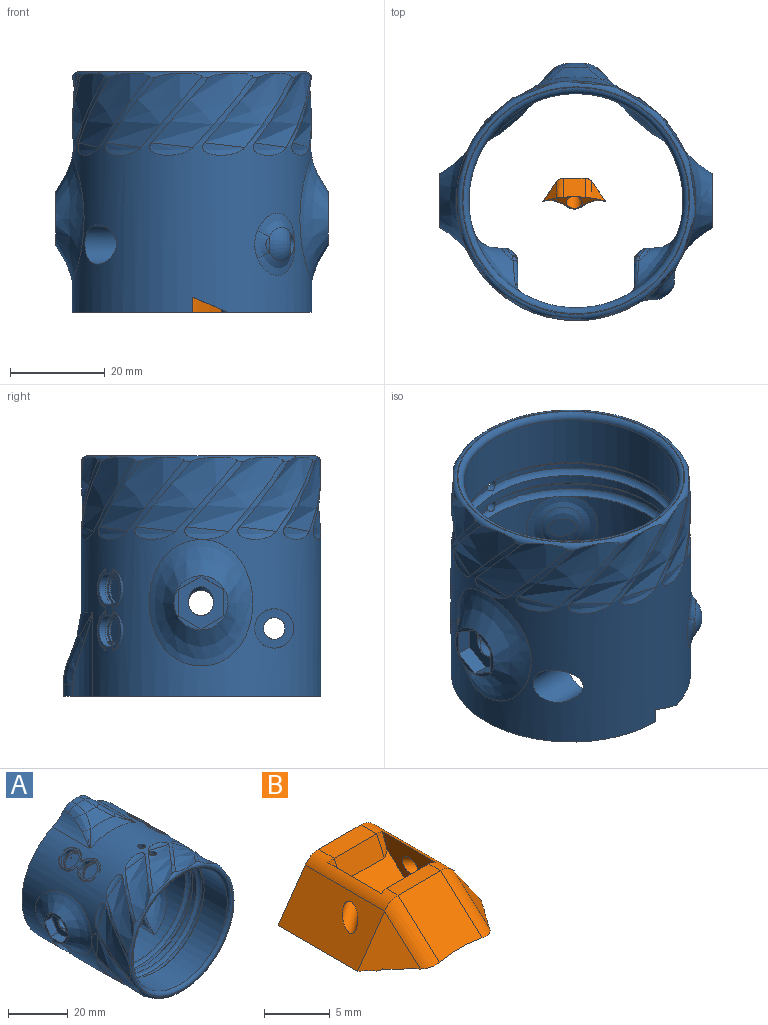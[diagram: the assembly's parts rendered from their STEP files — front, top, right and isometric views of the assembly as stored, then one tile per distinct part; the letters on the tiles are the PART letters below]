
ASSEMBLY  parts=2 mates=1
PART A: 254 faces, bbox 63.8x60.4x65 mm
  f0: cylinder r=3.37mm len=6.73mm, axis (0.64,0,0.77), area 10.5mm2, adj f1,f250,f251
  f1: torus R=20.91mm, axis (-0.55,-0.83,-0.04), area 47.7mm2, adj f0,f2,f3,f4,f249,f250
  f2: cylinder r=3.81mm len=7.62mm, axis (-0.64,0,-0.77), area 22.9mm2, adj f1,f3,f250
  f3: plane 7.63x5.85mm, normal (-0.64,0,-0.77), area 9.6mm2, adj f1,f2,f4
  f4: cylinder r=3.37mm len=6.73mm, axis (0.64,0,0.77), area 34.9mm2, adj f1,f3,f5,f7,f248
  f5: plane 9.44x3.14mm, normal (0.64,0,0.77), area 6.4mm2, adj f4,f6,f7
  f6: bspline ~8.68x3.45mm, area 0.1mm2, adj f5,f7
  f7: cylinder r=25.31mm len=50.62mm, axis (0,1,0), area 3905.4mm2, adj f4,f5,f6,f8,f168,f169,f170,f171
  f8: cylinder r=4.15mm len=11.06mm, axis (-1,0,0), area 190.1mm2, adj f7,f9,f161,f162,f163,f164,f165,f166
  f9: cylinder r=22.64mm len=45.29mm, axis (0,1,0), area 2204.6mm2, adj f8,f10,f32,f33,f34,f35,f50,f65
  f10: cylinder r=4.15mm len=8.31mm, axis (-1,0,0), area 147.8mm2, adj f9,f11,f24,f25,f26,f27,f28,f32
  f11: cylinder r=1.27mm len=1.9mm, axis (0,-1,0), area 0.9mm2, adj f10,f12,f24,f27
  f12: bspline ~1.21x1.2mm, area 0.4mm2, adj f11,f13,f23
  f13: bspline ~7.99x2.24mm, area 9.1mm2, adj f12,f14,f21,f22,f23,f27
  f14: cylinder r=5.42mm len=9.09mm, axis (-1,0,0), area 10.2mm2, adj f13,f15,f18,f33
  f15: torus R=4.41mm, axis (1,0,0), area 1.3mm2, adj f14,f16,f23,f24
  f16: bspline ~6.55x4.88mm, area 8.1mm2, adj f15,f17,f24,f33
  f17: bspline ~5.6x2.57mm, area 2.4mm2, adj f16,f32,f33
  f18: torus R=4.41mm, axis (1,0,0), area 1.3mm2, adj f14,f19,f21,f25
  f19: bspline ~6.55x4.88mm, area 8.1mm2, adj f18,f20,f25,f33
  f20: bspline ~4.89x2.08mm, area 2.4mm2, adj f19,f33,f34
  f21: bspline ~1.33x1.3mm, area 0.3mm2, adj f13,f18,f22,f25
  f22: bspline ~1.21x1.2mm, area 0.4mm2, adj f13,f21,f26
  f23: bspline ~1.05x0.91mm, area 0.3mm2, adj f12,f13,f15,f24
  f24: plane 5.75x4.22mm, normal (-1,0,0), area 6.7mm2, adj f10,f11,f15,f16,f23,f32
  f25: plane 5.74x4.21mm, normal (-1,0,0), area 6.7mm2, adj f10,f18,f19,f21,f26,f34
  f26: cylinder r=1.27mm len=1.9mm, axis (0,-1,0), area 0.9mm2, adj f10,f22,f25,f27
  f27: plane 6x1.48mm, normal (-0.71,0,0.71), area 5.5mm2, adj f10,f11,f13,f26
  f28: plane 8.31x8.31mm, normal (-1,0,0), area 37.8mm2, adj f10,f29
  f29: cylinder r=2.29mm len=4.57mm, axis (-1,0,0), area 44.4mm2, adj f28,f30,f168,f169,f170
  f30: torus R=0.85mm, axis (1,0,0), area 38mm2, adj f29,f31,f168,f170
  f31: cylinder r=5.42mm len=3.31mm, axis (-1,0,0), area 0mm2, adj f30,f171
  f32: cylinder r=1.52mm len=10.75mm, axis (0,1,0), area 11.5mm2, adj f9,f10,f17,f24
  f33: bspline ~24.01x16.87mm, area 259.2mm2, adj f9,f14,f16,f17,f19,f20,f34
  f34: cylinder r=1.52mm len=10.75mm, axis (0,1,0), area 10.8mm2, adj f9,f10,f20,f25,f33
  f35: cylinder r=5.71mm len=11.43mm, axis (1,0,0), area 14mm2, adj f9,f36
  f36: plane 17.21x17.21mm, normal (1,0,0), area 73.2mm2, adj f35,f37,f49
  f37: cylinder r=2.67mm len=5.33mm, axis (1,0,0), area 19.9mm2, adj f36,f38,f39,f49
  f38: cylinder r=2.63mm len=5.26mm, axis (-0.87,-0.49,0), area 0mm2, adj f37,f39
  f39: plane 14x12.51mm, normal (-1,0,0), area 55mm2, adj f37,f38,f40,f44,f45,f46,f47,f48
  f40: plane 5.17x3.77mm, normal (0,0.87,-0.5), area 19mm2, adj f39,f41,f43,f44,f48
  f41: plane 11.87x11.87mm, normal (-1,0,0), area 21.8mm2, adj f40,f42,f43,f44,f45,f46,f47,f48
  f42: cylinder r=2.63mm len=1.05mm, axis (-0.87,-0.49,0), area 0mm2, adj f41,f44
  f43: cylinder r=2.63mm len=1.05mm, axis (-0.87,-0.49,0), area 0mm2, adj f40,f41
  f44: plane 5.11x3.71mm, normal (0,0.87,0.5), area 19mm2, adj f39,f40,f41,f42,f45
  f45: plane 5.57x3.43mm, normal (0,0,1), area 19.1mm2, adj f39,f41,f44,f46
  f46: plane 4.83x3.43mm, normal (0,-0.87,0.5), area 19.1mm2, adj f39,f41,f45,f47
  f47: plane 4.83x3.43mm, normal (0,-0.87,-0.5), area 19.1mm2, adj f39,f41,f46,f48
  f48: plane 5.57x3.43mm, normal (0,0,-1), area 19.1mm2, adj f39,f40,f41,f47
  f49: cylinder r=2.63mm len=5.26mm, axis (-0.87,-0.49,0), area 0mm2, adj f36,f37
  f50: cylinder r=5.71mm len=11.43mm, axis (1,0,0), area 14mm2, adj f9,f51
  f51: plane 17.21x17.21mm, normal (-1,0,0), area 73.2mm2, adj f50,f52,f53
  f52: cylinder r=2.63mm len=5.26mm, axis (0.87,-0.49,0), area 0mm2, adj f51,f53
  f53: cylinder r=2.67mm len=5.33mm, axis (1,0,0), area 19.9mm2, adj f51,f52,f54,f64
  f54: plane 14x12.51mm, normal (1,0,0), area 55mm2, adj f53,f55,f59,f60,f61,f62,f63,f64
  f55: plane 4.83x3.43mm, normal (0,-0.87,-0.5), area 19.1mm2, adj f54,f56,f59,f63
  f56: plane 11.92x11.92mm, normal (1,0,0), area 21.8mm2, adj f55,f57,f58,f59,f60,f61,f62,f63
  f57: cylinder r=2.63mm len=1.05mm, axis (0.87,-0.49,0), area 0mm2, adj f56,f62
  f58: cylinder r=2.63mm len=1.05mm, axis (0.87,-0.49,0), area 0mm2, adj f56,f61
  f59: plane 4.83x3.43mm, normal (0,-0.87,0.5), area 19.1mm2, adj f54,f55,f56,f60
  f60: plane 5.57x3.43mm, normal (0,0,1), area 19.1mm2, adj f54,f56,f59,f61
  f61: plane 5.17x3.77mm, normal (0,0.87,0.5), area 19mm2, adj f54,f56,f58,f60,f62
  f62: plane 5.11x3.71mm, normal (0,0.87,-0.5), area 19mm2, adj f54,f56,f57,f61,f63
  f63: plane 5.57x3.43mm, normal (0,0,-1), area 19.1mm2, adj f54,f55,f56,f62
  f64: cylinder r=2.63mm len=5.26mm, axis (0.87,-0.49,0), area 0mm2, adj f53,f54
  f65: torus R=23.03mm, axis (0,-1,0), area 25.4mm2, adj f9,f66,f246,f247
  f66: bspline ~3.15x2.37mm, area 1.3mm2, adj f65,f67,f73,f247
  f67: bspline ~13.04x11.86mm, area 11.2mm2, adj f66,f68,f72,f247
  f68: bspline ~35.8x17.93mm, area 139.6mm2, adj f67,f69,f71,f73,f88
  f69: bspline ~3.19x1.63mm, area 2.1mm2, adj f68,f70,f75,f88
  f70: bspline ~4.55x2.66mm, area 4.6mm2, adj f69,f71,f74,f75
  f71: bspline ~4.25x3.15mm, area 6.9mm2, adj f68,f70,f74
  f72: bspline ~2.23x0.82mm, area 0.6mm2, adj f67,f88,f89,f247
  f73: bspline ~19.65x5.91mm, area 17.5mm2, adj f9,f66,f68,f74
  f74: bspline ~1.37x1.08mm, area 0.8mm2, adj f9,f70,f71,f73
  f75: bspline ~24.01x16.87mm, area 247.8mm2, adj f9,f69,f70,f76,f77,f85,f86,f87
  f76: bspline ~4.89x2.08mm, area 2.4mm2, adj f75,f77,f161
  f77: bspline ~6.55x4.88mm, area 8.1mm2, adj f75,f76,f78,f162
  f78: torus R=4.41mm, axis (1,0,0), area 1.3mm2, adj f77,f79,f85,f162
  f79: bspline ~1.28x1.27mm, area 0.3mm2, adj f78,f80,f81,f162
  f80: bspline ~1.21x1.2mm, area 0.4mm2, adj f79,f81,f163
  f81: bspline ~7.99x2.24mm, area 9.1mm2, adj f79,f80,f82,f83,f85,f164
  f82: bspline ~1.21x1.2mm, area 0.4mm2, adj f81,f83,f165
  f83: bspline ~1.33x1.3mm, area 0.3mm2, adj f81,f82,f84,f166
  f84: torus R=4.41mm, axis (1,0,0), area 1.3mm2, adj f83,f85,f86,f166
  f85: cylinder r=5.42mm len=9.09mm, axis (-1,0,0), area 10.2mm2, adj f75,f78,f81,f84
  f86: bspline ~6.55x4.88mm, area 8.1mm2, adj f75,f84,f87,f166
  f87: bspline ~5.6x2.57mm, area 2.4mm2, adj f75,f86,f167
  f88: bspline ~29.98x15.71mm, area 33.2mm2, adj f9,f68,f69,f72
  f89: torus R=23.03mm, axis (0,-1,0), area 1.1mm2, adj f9,f72,f90,f247
  f90: plane 8.88x4.76mm, normal (0.82,0,-0.57), area 41mm2, adj f9,f89,f91,f107,f108,f109,f247
  f91: plane 0.89x0.87mm, normal (-0.23,-0.65,0.72), area 0.3mm2, adj f90,f92,f107,f117
  f92: plane 4.06x3.42mm, normal (-0.16,-0.99,0.04), area 1.4mm2, adj f91,f93,f106,f107,f117
  f93: plane 8.23x0.69mm, normal (0,-0.74,-0.67), area 0.7mm2, adj f92,f94,f97,f98,f105,f106,f108,f117
  f94: plane 4.06x3.42mm, normal (0.16,-0.99,0.04), area 1.4mm2, adj f93,f95,f96,f97,f148
  f95: plane 0.89x0.87mm, normal (0.23,-0.65,0.72), area 0.3mm2, adj f94,f96,f148,f249
  f96: plane 4.19x2.94mm, normal (0.73,-0.46,0.51), area 1mm2, adj f94,f95,f97,f98,f249
  f97: extruded ~0.4x0.32mm, area 0mm2, adj f93,f94,f96,f98
  f98: cylinder r=2.03mm len=8.49mm, axis (0,1,0), area 14.4mm2, adj f93,f96,f97,f99,f102,f103,f104,f105
  f99: plane 5.9x0.63mm, normal (0,0.67,-0.74), area 3.7mm2, adj f98,f100,f101,f102,f105,f108
  f100: cylinder r=1.27mm len=5.84mm, axis (-1,0,0), area 11.7mm2, adj f99,f101,f102,f103
  f101: plane 2.76x0.85mm, normal (1,0,0), area 1.5mm2, adj f99,f100,f103,f108
  f102: plane 2.76x0.85mm, normal (-1,0,0), area 1.5mm2, adj f98,f99,f100,f103
  f103: plane 5.89x0.48mm, normal (0,-0.74,-0.67), area 2.6mm2, adj f98,f100,f101,f102,f104,f108
  f104: plane 4.57x4.45mm, normal (0,0,-1), area 20.3mm2, adj f98,f103,f108,f247
  f105: plane 4.57x1.49mm, normal (0,0,-1), area 6.8mm2, adj f93,f98,f99,f108
  f106: extruded ~0.4x0.32mm, area 0mm2, adj f92,f93,f107,f108
  f107: plane 4.19x2.94mm, normal (-0.73,-0.46,0.51), area 1mm2, adj f90,f91,f92,f106,f108
  f108: cylinder r=2.03mm len=8.49mm, axis (0,1,0), area 14.4mm2, adj f90,f93,f99,f101,f103,f104,f105,f106
  f109: torus R=20.91mm, axis (0.55,-0.83,-0.04), area 47.7mm2, adj f90,f110,f114,f115,f116,f184
  f110: cylinder r=3.37mm len=6.73mm, axis (-0.64,0,0.77), area 10.3mm2, adj f109,f111,f114
  f111: plane 6.73x5.16mm, normal (-0.64,0,0.77), area 35.5mm2, adj f110,f112,f113
  f112: plane 0.45x0.13mm, normal (0.56,0.34,0.75), area 0mm2, adj f111,f113
  f113: torus R=20.91mm, axis (0.55,-0.83,-0.04), area 0.1mm2, adj f111,f112
  f114: plane 7.62x5.84mm, normal (-0.64,0,0.77), area 9.5mm2, adj f109,f110,f115
  f115: cylinder r=3.81mm len=7.62mm, axis (-0.64,0,0.77), area 22.9mm2, adj f109,f114,f116
  f116: plane 7.63x5.85mm, normal (0.64,0,-0.77), area 9.6mm2, adj f109,f115,f184
  f117: plane 5.1x5.03mm, normal (0.73,0.46,-0.51), area 16.4mm2, adj f9,f91,f92,f93,f118
  f118: extruded ~5.22x4.81mm, area 11.5mm2, adj f9,f93,f117,f146
  f119: bspline ~14.5x11.6mm, area 84.2mm2, adj f9,f120,f126
  f120: bspline ~9.25x6.81mm, area 40.2mm2, adj f119,f121,f122
  f121: plane 4.62x4.52mm, normal (0.64,0,-0.77), area 21.6mm2, adj f120,f122
  f122: bspline ~4.17x3.65mm, area 6.9mm2, adj f120,f121,f123
  f123: bspline ~4.22x3.72mm, area 6.9mm2, adj f122,f124,f125
  f124: bspline ~9.25x6.81mm, area 40.2mm2, adj f123,f125,f126
  f125: plane 4.62x4.52mm, normal (0.64,0,-0.77), area 21.6mm2, adj f123,f124
  f126: bspline ~14.2x11.6mm, area 84.2mm2, adj f9,f119,f124,f135
  f127: bspline ~14.5x11.61mm, area 84.2mm2, adj f9,f128,f134
  f128: bspline ~9.25x6.81mm, area 40.2mm2, adj f127,f129,f130
  f129: plane 4.62x4.52mm, normal (-0.64,0,-0.77), area 21.6mm2, adj f128,f130
  f130: bspline ~4.17x3.68mm, area 6.9mm2, adj f128,f129,f131
  f131: bspline ~4.22x3.7mm, area 6.9mm2, adj f130,f132,f133
  f132: bspline ~9.25x6.81mm, area 40.2mm2, adj f131,f133,f134
  f133: plane 4.62x4.52mm, normal (-0.64,0,-0.77), area 21.6mm2, adj f131,f132
  f134: bspline ~14.2x11.6mm, area 84.2mm2, adj f9,f127,f132,f135
  f135: torus R=22.14mm, axis (0,1,0), area 243.9mm2, adj f9,f126,f134,f136,f242
  f136: cylinder r=23.81mm len=47.63mm, axis (0,1,0), area 174.6mm2, adj f135,f137,f242
  f137: torus R=22.14mm, axis (0,1,0), area 244.3mm2, adj f136,f138,f242
  f138: cylinder r=22.64mm len=45.29mm, axis (0,1,0), area 274.1mm2, adj f137,f139
  f139: torus R=22.14mm, axis (0,1,0), area 244.3mm2, adj f138,f140,f145
  f140: cylinder r=23.81mm len=47.63mm, axis (0,1,0), area 174.5mm2, adj f139,f141,f145
  f141: torus R=22.14mm, axis (0,1,0), area 244.3mm2, adj f140,f142,f145
  f142: cylinder r=22.64mm len=45.29mm, axis (0,1,0), area 1564.5mm2, adj f141,f143
  f143: torus R=23.91mm, axis (0,1,0), area 289.6mm2, adj f142,f144
  f144: plane 48.08x48.08mm, normal (0,-1,0), area 19.1mm2, adj f143,f236
  f145: cylinder r=1.27mm len=2.54mm, axis (0,0,-1), area 10.9mm2, adj f139,f140,f141,f240
  f146: plane 4.93x4.71mm, normal (0,0.67,-0.74), area 29mm2, adj f9,f93,f118,f147
  f147: extruded ~5.22x4.81mm, area 11.5mm2, adj f9,f93,f146,f148
  f148: plane 5.1x5.03mm, normal (-0.73,0.46,-0.51), area 16.4mm2, adj f9,f93,f94,f95,f147
  f149: torus R=23.03mm, axis (0,-1,0), area 20.1mm2, adj f9,f150,f247,f249
  f150: bspline ~3.31x2.12mm, area 1.3mm2, adj f149,f151,f155,f247
  f151: bspline ~13.96x10.82mm, area 11.2mm2, adj f150,f152,f154,f247
  f152: bspline ~36.8x15.68mm, area 139.5mm2, adj f151,f153,f155,f159
  f153: bspline ~4.22x3.05mm, area 6.5mm2, adj f152,f156,f157,f158
  f154: bspline ~2.21x0.95mm, area 0.6mm2, adj f151,f159,f160,f247
  f155: bspline ~20.64x6.24mm, area 17.5mm2, adj f9,f150,f152,f156
  f156: bspline ~2.9x1.48mm, area 2.5mm2, adj f9,f153,f155,f157
  f157: bspline ~1.21x0.88mm, area 0.6mm2, adj f9,f153,f156,f158
  f158: bspline ~2.4x1.86mm, area 2.4mm2, adj f9,f153,f157,f159
  f159: bspline ~33.07x14.23mm, area 35.3mm2, adj f9,f152,f154,f158
  f160: torus R=23.03mm, axis (0,-1,0), area 2mm2, adj f9,f154,f245,f247
  f161: cylinder r=1.52mm len=10.75mm, axis (0,1,0), area 10.8mm2, adj f8,f9,f75,f76,f162
  f162: plane 5.75x4.22mm, normal (1,0,0), area 6.7mm2, adj f8,f77,f78,f79,f161,f163
  f163: cylinder r=1.27mm len=1.9mm, axis (0,-1,0), area 0.9mm2, adj f8,f80,f162,f164
  f164: plane 6x1.48mm, normal (0.71,0,0.71), area 5.5mm2, adj f8,f81,f163,f165
  f165: cylinder r=1.27mm len=1.9mm, axis (0,-1,0), area 0.9mm2, adj f8,f82,f164,f166
  f166: plane 5.74x4.21mm, normal (1,0,0), area 6.7mm2, adj f8,f83,f84,f86,f165,f167
  f167: cylinder r=1.52mm len=10.75mm, axis (0,1,0), area 11.5mm2, adj f8,f9,f87,f166
  f168: bspline ~8.2x8.04mm, area 33.9mm2, adj f7,f29,f30,f169,f171
  f169: cylinder r=4.57mm len=1.7mm, axis (0,1,0), area 0.2mm2, adj f7,f29,f168,f170
  f170: bspline ~8.09x7.87mm, area 33.9mm2, adj f7,f29,f30,f169,f171
  f171: bspline ~7.72x3.76mm, area 13.3mm2, adj f7,f31,f168,f170
  f172: bspline ~8.68x3.09mm, area 0.1mm2, adj f7,f173
  f173: plane 9.44x3.14mm, normal (-0.64,0,0.77), area 6.4mm2, adj f7,f172,f174
  f174: cylinder r=3.37mm len=6.73mm, axis (-0.64,0,0.77), area 35.1mm2, adj f7,f173,f175,f180
  f175: plane 7.62x5.84mm, normal (0.64,0,-0.77), area 10mm2, adj f174,f176
  f176: cylinder r=3.81mm len=7.62mm, axis (-0.64,0,0.77), area 24.3mm2, adj f175,f177
  f177: plane 7.62x5.84mm, normal (-0.64,0,0.77), area 10mm2, adj f176,f178
  f178: cylinder r=3.37mm len=6.73mm, axis (-0.64,0,0.77), area 10.5mm2, adj f177,f179
  f179: plane 6.73x5.16mm, normal (-0.64,0,0.77), area 35.6mm2, adj f178
  f180: plane 9.44x3.14mm, normal (-0.64,0,0.77), area 6.4mm2, adj f7,f174,f181
  f181: bspline ~8.68x3.45mm, area 0.1mm2, adj f7,f180
  f182: bspline ~8.68x3.09mm, area 0.1mm2, adj f7,f183
  f183: plane 9.44x3.14mm, normal (-0.64,0,0.77), area 6.4mm2, adj f7,f182,f184
  f184: cylinder r=3.37mm len=6.73mm, axis (-0.64,0,0.77), area 35.1mm2, adj f7,f109,f116,f183,f185
  f185: plane 9.44x3.14mm, normal (-0.64,0,0.77), area 6.4mm2, adj f7,f184,f186
  f186: bspline ~8.68x3.45mm, area 0.1mm2, adj f7,f185
  f187: bspline ~8.68x3.45mm, area 0.1mm2, adj f7,f188
  f188: plane 9.44x3.14mm, normal (0.64,0,0.77), area 6.4mm2, adj f7,f187,f189
  f189: cylinder r=3.37mm len=6.73mm, axis (0.64,0,0.77), area 34.9mm2, adj f7,f188,f190,f195
  f190: plane 7.62x5.84mm, normal (-0.64,0,-0.77), area 10mm2, adj f189,f191
  f191: cylinder r=3.81mm len=7.62mm, axis (-0.64,0,-0.77), area 24.3mm2, adj f190,f192
  f192: plane 7.62x5.84mm, normal (0.64,0,0.77), area 10mm2, adj f191,f193
  f193: cylinder r=3.37mm len=6.73mm, axis (0.64,0,0.77), area 10.7mm2, adj f192,f194
  f194: plane 6.73x5.16mm, normal (0.64,0,0.77), area 35.6mm2, adj f193
  f195: plane 9.44x3.14mm, normal (0.64,0,0.77), area 6.4mm2, adj f7,f189,f196
  f196: bspline ~8.68x3.09mm, area 0.1mm2, adj f7,f195
  f197: bspline ~8.68x3.09mm, area 0.1mm2, adj f7,f248
  f198: bspline ~26.69x21.89mm, area 456.4mm2, adj f7,f41
  f199: bspline ~26.69x21.9mm, area 456.4mm2, adj f7,f56
  f200: cylinder r=13.97mm len=17.77mm, axis (0,1,0), area 75.7mm2, adj f7,f201,f209,f210,f211,f247
  f201: bspline ~7.83x4.14mm, area 18.1mm2, adj f200,f202,f209,f211
  f202: torus R=15.15mm, axis (0,-1,0), area 22.5mm2, adj f201,f203,f207,f208
  f203: bspline ~9.36x4.49mm, area 18.1mm2, adj f202,f204,f205,f244
  f204: cylinder r=5.08mm len=3.7mm, axis (0,-1,0), area 11mm2, adj f203,f208,f244,f247
  f205: bspline ~9.02x6.04mm, area 23.3mm2, adj f203,f206,f207,f244
  f206: bspline ~6.69x5.34mm, area 7.6mm2, adj f205,f243,f244
  f207: cone r=29.12mm half-angle=20.6deg, axis (0,1,0), area 46.9mm2, adj f202,f205,f211,f243
  f208: cylinder r=29.12mm len=3.9mm, axis (0,1,0), area 9.9mm2, adj f202,f204,f209,f247
  f209: cylinder r=5.08mm len=3.7mm, axis (0,1,0), area 11mm2, adj f200,f201,f208,f247
  f210: bspline ~6.69x5.34mm, area 7.6mm2, adj f200,f211,f243
  f211: bspline ~10.91x6.7mm, area 23.3mm2, adj f200,f201,f207,f210
  f212: bspline ~11.18x3.36mm, area 16.8mm2, adj f7,f213
  f213: bspline ~22.76x17.78mm, area 139.2mm2, adj f7,f212,f236
  f214: bspline ~9x7.65mm, area 16.8mm2, adj f7,f215
  f215: bspline ~21.44x17.78mm, area 139.2mm2, adj f7,f214,f236
  f216: bspline ~10.58x5.07mm, area 16.8mm2, adj f7,f217
  f217: bspline ~25.8x17.78mm, area 139.2mm2, adj f7,f216,f236
  f218: bspline ~11.53x3.13mm, area 16.8mm2, adj f7,f219
  f219: bspline ~25.05x17.78mm, area 139.2mm2, adj f7,f218,f236
  f220: bspline ~10.33x5.64mm, area 16.8mm2, adj f7,f221
  f221: bspline ~19.34x17.78mm, area 139.2mm2, adj f7,f220,f236
  f222: bspline ~9.35x7.21mm, area 16.8mm2, adj f7,f223
  f223: bspline ~24.23x17.78mm, area 139.2mm2, adj f7,f222,f236
  f224: bspline ~11.31x3.13mm, area 16.8mm2, adj f7,f225
  f225: bspline ~26.08x17.78mm, area 139.2mm2, adj f7,f224,f236
  f226: bspline ~11.18x3.36mm, area 16.8mm2, adj f7,f227
  f227: bspline ~22.76x17.78mm, area 139.2mm2, adj f7,f226,f236
  f228: bspline ~9x7.65mm, area 16.8mm2, adj f7,f229
  f229: bspline ~21.44x17.78mm, area 139.2mm2, adj f7,f228,f236
  f230: bspline ~10.58x5.07mm, area 16.8mm2, adj f7,f231
  f231: bspline ~25.8x17.78mm, area 139.2mm2, adj f7,f230,f236
  f232: bspline ~11.53x3.13mm, area 16.8mm2, adj f7,f233
  f233: bspline ~25.05x17.78mm, area 139.2mm2, adj f7,f232,f236
  f234: bspline ~10.33x5.64mm, area 16.8mm2, adj f7,f235
  f235: bspline ~19.34x17.78mm, area 139.2mm2, adj f7,f234,f236
  f236: torus R=24.04mm, axis (0,1,0), area 190.8mm2, adj f7,f144,f213,f215,f217,f219,f221,f223
  f237: bspline ~9.35x7.21mm, area 16.8mm2, adj f7,f238
  f238: bspline ~24.23x17.78mm, area 143.6mm2, adj f7,f236,f237,f239
  f239: cylinder r=25.31mm len=3.74mm, axis (0,1,0), area 4.5mm2, adj f7,f236,f238,f240
  f240: bspline ~26.08x17.78mm, area 134mm2, adj f7,f145,f236,f239,f241
  f241: bspline ~11.31x3.13mm, area 16.8mm2, adj f7,f240
  f242: cylinder r=1.27mm len=2.54mm, axis (0,0,-1), area 13.3mm2, adj f7,f135,f136,f137
  f243: torus R=39.28mm, axis (0,1,0), area 83.4mm2, adj f7,f206,f207,f210
  f244: cylinder r=13.97mm len=17.77mm, axis (0,1,0), area 75.7mm2, adj f7,f203,f204,f205,f206,f247
  f245: plane 7.66x3.82mm, normal (-0.38,0.92,0), area 22.3mm2, adj f7,f9,f160,f246,f247
  f246: plane 3.18x2.67mm, normal (1,0,0), area 8.4mm2, adj f7,f9,f65,f245,f247
  f247: plane 54.43x50.62mm, normal (0,1,0), area 284.5mm2, adj f7,f65,f66,f67,f72,f89,f90,f98
  f248: plane 9.44x3.14mm, normal (0.64,0,0.77), area 6.4mm2, adj f4,f7,f197
  f249: plane 8.83x4.71mm, normal (-0.82,0,-0.57), area 41mm2, adj f1,f9,f95,f96,f98,f149,f247
  f250: plane 7.62x5.84mm, normal (0.64,0,0.77), area 9.5mm2, adj f0,f1,f2
  f251: plane 6.73x5.16mm, normal (0.64,0,0.77), area 35.5mm2, adj f0,f252,f253
  f252: plane 0.45x0.13mm, normal (-0.56,0.34,0.75), area 0mm2, adj f251,f253
  f253: torus R=20.91mm, axis (-0.55,-0.83,-0.04), area 0.1mm2, adj f251,f252
PART B: 32 faces, bbox 13.8x13.3x8 mm
  f0: plane 4.86x2.14mm, normal (0,-0.74,-0.67), area 4.2mm2, adj f1,f5,f29
  f1: cylinder r=22.64mm len=11.04mm, axis (0,1,0), area 21.6mm2, adj f0,f5,f16,f17,f18,f19,f20,f24
  f2: cylinder r=22.64mm len=13.32mm, axis (0,1,0), area 71.9mm2, adj f10,f11,f15,f16,f20,f26
  f3: plane 6.08x2.54mm, normal (0,-0.67,0.74), area 15.4mm2, adj f4,f6,f8,f21,f22,f23
  f4: plane 5.84x3.39mm, normal (0,0.74,0.67), area 17.9mm2, adj f3,f5,f6,f8,f9
  f5: cylinder r=1.68mm len=5.85mm, axis (0,-0.74,-0.67), area 51.1mm2, adj f0,f1,f4,f24,f28
  f6: plane 6.11x3.72mm, normal (-1,0,0), area 9.4mm2, adj f3,f4,f9,f14,f21,f30
  f7: plane 4.57x1.68mm, normal (0,0,1), area 7.7mm2, adj f10,f12,f14,f22
  f8: plane 6.11x3.72mm, normal (1,0,0), area 9.4mm2, adj f3,f4,f9,f12,f23,f31
  f9: plane 5.91x0.26mm, normal (0,0.67,-0.74), area 1.5mm2, adj f4,f6,f8,f12,f13,f14
  f10: plane 13.32x4.93mm, normal (0,1,0), area 39.5mm2, adj f2,f7,f11,f12,f14,f15
  f11: plane 8.56x4.17mm, normal (-0.82,0,0.57), area 40.7mm2, adj f2,f10,f12,f16,f31
  f12: cylinder r=1.78mm len=8.56mm, axis (0,1,0), area 10.9mm2, adj f7,f8,f9,f10,f11,f13,f17,f23
  f13: plane 4.57x1.28mm, normal (0,0,1), area 5.8mm2, adj f9,f12,f14,f18
  f14: cylinder r=1.78mm len=8.56mm, axis (0,1,0), area 10.9mm2, adj f6,f7,f9,f10,f13,f15,f19,f21
  f15: plane 8.56x4.17mm, normal (0.82,0,0.57), area 40.8mm2, adj f2,f10,f14,f20,f30
  f16: plane 4.22x3.9mm, normal (-0.73,-0.46,0.51), area 10.9mm2, adj f1,f2,f11,f17,f26,f27
  f17: extruded ~4.85x4.46mm, area 9mm2, adj f1,f12,f16,f18
  f18: plane 4.57x4.47mm, normal (0,-0.67,0.74), area 27mm2, adj f1,f13,f17,f19
  f19: extruded ~4.85x4.46mm, area 9mm2, adj f1,f14,f18,f20
  f20: plane 4.22x3.9mm, normal (0.73,-0.46,0.51), area 10.9mm2, adj f1,f2,f15,f19,f26,f29
  f21: bspline ~2.18x1.54mm, area 1.2mm2, adj f3,f6,f14,f22
  f22: plane 4.57x1.83mm, normal (0,-0.91,0.41), area 9.2mm2, adj f3,f7,f21,f23
  f23: bspline ~2.18x1.54mm, area 1.2mm2, adj f3,f8,f12,f22
  f24: plane 4.86x2.14mm, normal (0,-0.74,-0.67), area 4.2mm2, adj f1,f5,f27
  f25: cylinder r=2.18mm len=2.86mm, axis (0,0.74,0.67), area 4.6mm2, adj f26,f28
  f26: bspline ~13.51x7.89mm, area 47.8mm2, adj f2,f16,f20,f25,f27,f29
  f27: bspline ~5.61x2.35mm, area 3mm2, adj f1,f16,f24,f26,f28
  f28: torus R=1.68mm, axis (0,0.74,0.67), area 2.3mm2, adj f5,f25,f27,f29
  f29: bspline ~5.61x2.35mm, area 3mm2, adj f0,f1,f20,f26,f28
  f30: torus R=20.91mm, axis (-0.55,-0.83,-0.04), area 9.7mm2, adj f6,f15
  f31: torus R=20.91mm, axis (0.55,-0.83,-0.04), area 9.7mm2, adj f8,f11
PLACE A rot(axis=(-1,0,0),90deg) t=(-25.58,10.52,17.72)mm
PLACE B rot(axis=(-1,0,0),90deg) t=(-25.95,-11.23,17.72)mm
MATE planar B.f10 <-> A.f247  axis (0,0,-1) through (-25.95,12.97,-15.55)mm
